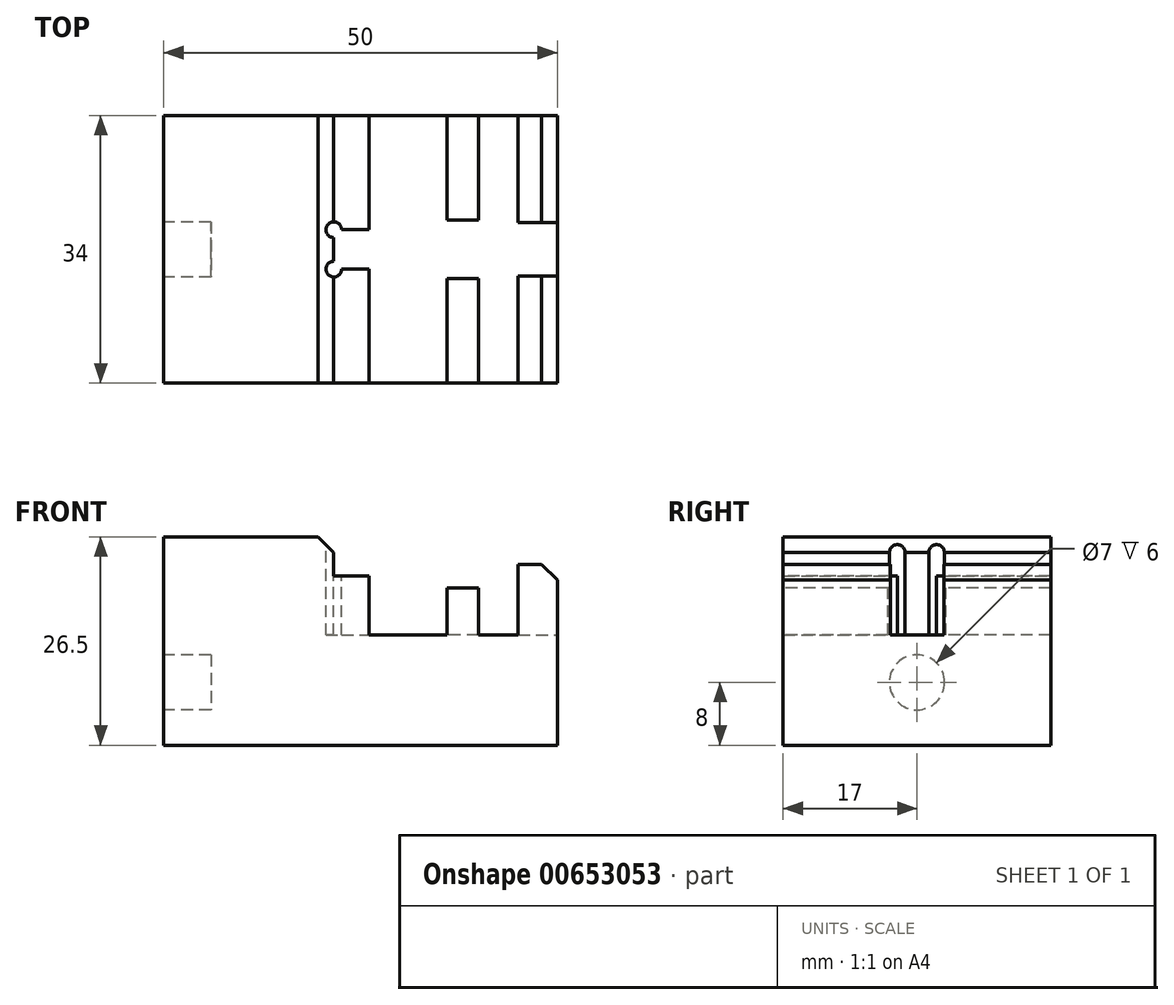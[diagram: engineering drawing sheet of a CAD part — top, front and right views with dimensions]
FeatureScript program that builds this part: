
annotation { "Feature Type Name" : "Feature", "Feature Type Description" : "" }
export const myFeature = defineFeature(function(context is Context, id is Id, definition is map)
    precondition{}
    {
        {
            var Q0;
            Q0=qCreatedBy(makeId("Front.planeOp"),FACE);
            var sketch = newSketch(context, id + "F0", { "sketchPlane" : qUnion([Q0])});
            skLineSegment(sketch, "E0.bottom", {"start": v(-25, 13) * mm, "end": v(-3.4, 13) * mm});
            skLineSegment(sketch, "E0.top", {"start": v(-25, -13) * mm, "end": v(25, -13) * mm});
            skLineSegment(sketch, "E0.left", {"start": v(-25, 13) * mm, "end": v(-25, -13) * mm});
            skLineSegment(sketch, "E0.right", {"start": v(25, 10) * mm, "end": v(25, -13) * mm});
            skPoint(sketch, "E0.middle", {"position": v(0, 0) * mm});
            skLineSegment(sketch, "E1.0", {"start": v(-3.4, 13) * mm, "end": v(-3.4, 1) * mm});
            skLineSegment(sketch, "E2.0", {"start": v(-3.4, 1) * mm, "end": v(20, 1) * mm});
            skLineSegment(sketch, "E3.0", {"start": v(20, 10) * mm, "end": v(20, 1) * mm});
            skPoint(sketch, "E4.orphan", {"position": v(25, 13) * mm});
            skLineSegment(sketch, "E5.trimOffspring", {"start": v(20, 10) * mm, "end": v(25, 10) * mm});
            skSolve(sketch);
        }
        {
            var Q0;
            Q0=qSketchRegion(id+"F0",true);
            extrude(context, id + "F1", {"entities" : qUnion([Q0]), "depth" : 34 * mm, "offsetDistance" : 25 * mm});
        }
        {
            var Q0;
            Q0=makeQuery(id+"F1.opExtrude","SWEPT_FACE",FACE,{"disambiguationData":[OSD([sQuery(id+"F0.wireOp",EDGE,"E0.right")])]});
            var sketch = newSketch(context, id + "F2", { "sketchPlane" : qUnion([Q0])});
            skLineSegment(sketch, "E6.bottom", {"start": v(-20.4, 10) * mm, "end": v(-13.6, 10) * mm});
            skLineSegment(sketch, "E6.top", {"start": v(-20.4, 1) * mm, "end": v(-13.6, 1) * mm});
            skLineSegment(sketch, "E6.left", {"start": v(-20.4, 10) * mm, "end": v(-20.4, 1) * mm});
            skLineSegment(sketch, "E6.right", {"start": v(-13.6, 10) * mm, "end": v(-13.6, 1) * mm});
            skSolve(sketch);
        }
        {
            var Q0;
            Q0=qSketchRegion(id+"F2",true);
            var Q1;
            Q1=makeQuery(id+"F1.opExtrude","SWEPT_FACE",FACE,{"disambiguationData":[OSD([sQuery(id+"F0.wireOp",EDGE,"E3.0")])]});
            extrude(context, id + "F3", {"entities" : qUnion([Q0]), "operationType" : NewBodyOperationType.REMOVE, "endBound" : BoundingType.UP_TO_SURFACE, "oppositeDirection" : true, "depth" : 25 * mm, "endBoundEntityFace" : qUnion([Q1]), "offsetDistance" : 25 * mm});
        }
        {
            var Q0;
            Q0=makeQuery(id+"F1.opExtrude","SWEPT_FACE",FACE,{"disambiguationData":[OSD([sQuery(id+"F0.wireOp",EDGE,"E0.left")])]});
            var sketch = newSketch(context, id + "F4", { "sketchPlane" : qUnion([Q0])});
            skCircle(sketch, "E7", {"center": v(17, -5) * mm, "radius": 3.5 * mm});
            skSolve(sketch);
        }
        {
            var Q0;
            Q0=qSketchRegion(id+"F4",true);
            extrude(context, id + "F5", {"entities" : qUnion([Q0]), "operationType" : NewBodyOperationType.REMOVE, "oppositeDirection" : true, "depth" : 6 * mm, "offsetDistance" : 25 * mm});
        }
        {
            var Q0;
            Q0=makeQuery(id+"F3.boolean.opBoolean","MERGE",FACE,{"derivedFrom":[makeQuery(id+"F1.opExtrude","SWEPT_FACE",FACE,{"disambiguationData":[OSD([sQuery(id+"F0.wireOp",EDGE,"E2.0")])]}),makeQuery(id+"F3.opExtrude","SWEPT_FACE",FACE,{"disambiguationData":[OSD([sQuery(id+"F2.wireOp",EDGE,"E6.top")])]})]});
            var sketch = newSketch(context, id + "F6", { "sketchPlane" : qUnion([Q0])});
            skLineSegment(sketch, "E8.bottom", {"start": v(-3.4, -34) * mm, "end": v(1.1, -34) * mm});
            skLineSegment(sketch, "E8.top", {"start": v(-3.4, -19.5) * mm, "end": v(1.1, -19.5) * mm});
            skLineSegment(sketch, "E8.left", {"start": v(-3.4, -34) * mm, "end": v(-3.4, -19.5) * mm});
            skLineSegment(sketch, "E8.right", {"start": v(1.1, -34) * mm, "end": v(1.1, -19.5) * mm});
            skLineSegment(sketch, "E9.bottom", {"start": v(-3.4, 0) * mm, "end": v(1.1, 0) * mm});
            skLineSegment(sketch, "E9.top", {"start": v(-3.4, -14.5) * mm, "end": v(1.1, -14.5) * mm});
            skLineSegment(sketch, "E9.left", {"start": v(-3.4, 0) * mm, "end": v(-3.4, -14.5) * mm});
            skLineSegment(sketch, "E9.right", {"start": v(1.1, 0) * mm, "end": v(1.1, -14.5) * mm});
            skSolve(sketch);
        }
        {
            var Q0;
            Q0 = qSketchRegion(id + "F6", true);
            var Q1;
            Q1=makeQuery(id+"F1.opExtrude","SWEPT_FACE",FACE,{"disambiguationData":[OSD([sQuery(id+"F0.wireOp",EDGE,"E0.bottom")])]});
            extrude(context, id + "F7", {"entities" : qUnion([Q0]), "operationType" : NewBodyOperationType.ADD, "endBound" : BoundingType.UP_TO_SURFACE, "depth" : 25 * mm, "endBoundEntityFace" : qUnion([Q1]), "offsetDistance" : 25 * mm});
        }
        {
            var Q0;
            {var subQ0=sQuery(id+"F0.wireOp",EDGE,"E0.bottom");Q0=makeQuery(id+"F7.boolean.opBoolean","MERGE",FACE,{"derivedFrom":[makeQuery(id+"F1.opExtrude","SWEPT_FACE",FACE,{"disambiguationData":[OSD([subQ0])]}),makeQuery(id+"F7.opExtrude","CAP_FACE",FACE,{"disambiguationData":[OSD([subQ0]),OD(0.0)],"isStart":false}),makeQuery(id+"F7.opExtrude","CAP_FACE",FACE,{"disambiguationData":[OSD([subQ0]),OD(1.0)],"isStart":false})]});}
            var sketch = newSketch(context, id + "F8", { "sketchPlane" : qUnion([Q0])});
            skLineSegment(sketch, "E10.top", {"start": v(1.1, -21.7) * mm, "end": v(11, -21.7) * mm});
            skLineSegment(sketch, "E11.top", {"start": v(1.1, -12.3) * mm, "end": v(11, -12.3) * mm});
            skLineSegment(sketch, "E12.top", {"start": v(1.1, -34) * mm, "end": v(11, -34) * mm});
            skLineSegment(sketch, "E12.left", {"start": v(1.1, -21.7) * mm, "end": v(1.1, -34) * mm});
            skLineSegment(sketch, "E12.right", {"start": v(11, -21.7) * mm, "end": v(11, -34) * mm});
            skLineSegment(sketch, "E13.top", {"start": v(1.1, 0) * mm, "end": v(11, 0) * mm});
            skLineSegment(sketch, "E13.left", {"start": v(1.1, -12.3) * mm, "end": v(1.1, 0) * mm});
            skLineSegment(sketch, "E13.right", {"start": v(11, -12.3) * mm, "end": v(11, 0) * mm});
            skSolve(sketch);
        }
        {
            var Q0;
            Q0 = qSketchRegion(id + "F8", true);
            var Q1;
            Q1=makeQuery(id+"F3.boolean.opBoolean","MERGE",FACE,{"derivedFrom":[makeQuery(id+"F1.opExtrude","SWEPT_FACE",FACE,{"disambiguationData":[OSD([sQuery(id+"F0.wireOp",EDGE,"E2.0")])]}),makeQuery(id+"F3.opExtrude","SWEPT_FACE",FACE,{"disambiguationData":[OSD([sQuery(id+"F2.wireOp",EDGE,"E6.top")])]})]});
            extrude(context, id + "F9", {"entities" : qUnion([Q0]), "operationType" : NewBodyOperationType.ADD, "endBound" : BoundingType.UP_TO_SURFACE, "oppositeDirection" : true, "depth" : 25 * mm, "endBoundEntityFace" : qUnion([Q1]), "offsetDistance" : 25 * mm});
        }
        {
            var Q0;
            {var subQ0=sQuery(id+"F0.wireOp",EDGE,"E0.bottom");Q0=makeQuery(id+"F9.boolean.opBoolean","MERGE",FACE,{"derivedFrom":[makeQuery(id+"F7.boolean.opBoolean","MERGE",FACE,{"derivedFrom":[makeQuery(id+"F1.opExtrude","SWEPT_FACE",FACE,{"disambiguationData":[OSD([subQ0])]}),makeQuery(id+"F7.opExtrude","CAP_FACE",FACE,{"disambiguationData":[OSD([subQ0]),OD(0.0)],"isStart":false}),makeQuery(id+"F7.opExtrude","CAP_FACE",FACE,{"disambiguationData":[OSD([subQ0]),OD(1.0)],"isStart":false})]}),makeQuery(id+"F9.opExtrude","CAP_FACE",FACE,{"disambiguationData":[OSD([sQuery(id+"F8.wireOp",EDGE,"E10.top"),sQuery(id+"F8.wireOp",EDGE,"E12.top"),sQuery(id+"F8.wireOp",EDGE,"E12.left"),sQuery(id+"F8.wireOp",EDGE,"E12.right")])],"isStart":true}),makeQuery(id+"F9.opExtrude","CAP_FACE",FACE,{"disambiguationData":[OSD([sQuery(id+"F8.wireOp",EDGE,"E11.top"),sQuery(id+"F8.wireOp",EDGE,"E13.top"),sQuery(id+"F8.wireOp",EDGE,"E13.left"),sQuery(id+"F8.wireOp",EDGE,"E13.right")])],"isStart":true})]});}
            var sketch = newSketch(context, id + "F10", { "sketchPlane" : qUnion([Q0])});
            skLineSegment(sketch, "E14.bottom", {"start": v(11, -34) * mm, "end": v(15, -34) * mm});
            skLineSegment(sketch, "E14.top", {"start": v(11, -20.7) * mm, "end": v(15, -20.7) * mm});
            skLineSegment(sketch, "E14.left", {"start": v(11, -34) * mm, "end": v(11, -20.7) * mm});
            skLineSegment(sketch, "E14.right", {"start": v(15, -34) * mm, "end": v(15, -20.7) * mm});
            skLineSegment(sketch, "E15.MirrorCS", {"start": v(11, 0) * mm, "end": v(11, -13.3) * mm});
            skLineSegment(sketch, "E16.MirrorCS", {"start": v(15, 0) * mm, "end": v(15, -13.3) * mm});
            skLineSegment(sketch, "E17.MirrorCS", {"start": v(11, -13.3) * mm, "end": v(15, -13.3) * mm});
            skLineSegment(sketch, "E18.MirrorCS", {"start": v(11, 0) * mm, "end": v(15, 0) * mm});
            skSolve(sketch);
        }
        {
            var Q0;
            Q0 = qSketchRegion(id + "F10", true);
            var Q1;
            Q1=makeQuery(id+"F3.boolean.opBoolean","MERGE",FACE,{"derivedFrom":[makeQuery(id+"F1.opExtrude","SWEPT_FACE",FACE,{"disambiguationData":[OSD([sQuery(id+"F0.wireOp",EDGE,"E2.0")])]}),makeQuery(id+"F3.opExtrude","SWEPT_FACE",FACE,{"disambiguationData":[OSD([sQuery(id+"F2.wireOp",EDGE,"E6.top")])]})]});
            extrude(context, id + "F11", {"entities" : qUnion([Q0]), "operationType" : NewBodyOperationType.ADD, "endBound" : BoundingType.UP_TO_SURFACE, "oppositeDirection" : true, "depth" : 25 * mm, "endBoundEntityFace" : qUnion([Q1]), "offsetDistance" : 25 * mm});
        }
        {
            var Q0;
            Q0=makeQuery(id+"F11.boolean.opBoolean","MERGE",FACE,{"derivedFrom":[makeQuery(id+"F9.boolean.opBoolean","MERGE",FACE,{"derivedFrom":[makeQuery(id+"F7.boolean.opBoolean","MERGE",FACE,{"derivedFrom":[makeQuery(id+"F1.opExtrude","CAP_FACE",FACE,{"disambiguationData":[OSD([sQuery(id+"F0.wireOp",EDGE,"E0.bottom"),sQuery(id+"F0.wireOp",EDGE,"E0.top"),sQuery(id+"F0.wireOp",EDGE,"E0.left"),sQuery(id+"F0.wireOp",EDGE,"E0.right"),sQuery(id+"F0.wireOp",EDGE,"E1.0"),sQuery(id+"F0.wireOp",EDGE,"E2.0"),sQuery(id+"F0.wireOp",EDGE,"E3.0"),sQuery(id+"F0.wireOp",EDGE,"E5.trimOffspring")])],"isStart":false}),makeQuery(id+"F7.opExtrude","SWEPT_FACE",FACE,{"disambiguationData":[OSD([sQuery(id+"F6.wireOp",EDGE,"E8.bottom")])]})]}),makeQuery(id+"F9.opExtrude","SWEPT_FACE",FACE,{"disambiguationData":[OSD([sQuery(id+"F8.wireOp",EDGE,"E12.top")])]})]}),makeQuery(id+"F11.opExtrude","SWEPT_FACE",FACE,{"disambiguationData":[OSD([sQuery(id+"F10.wireOp",EDGE,"E14.bottom")])]})]});
            var sketch = newSketch(context, id + "F12", { "sketchPlane" : qUnion([Q0])});
            skLineSegment(sketch, "E19.bottom", {"start": v(15, 13) * mm, "end": v(1.1, 13) * mm});
            skLineSegment(sketch, "E19.top", {"start": v(15, 7) * mm, "end": v(1.1, 7) * mm});
            skLineSegment(sketch, "E19.left", {"start": v(15, 13) * mm, "end": v(15, 7) * mm});
            skLineSegment(sketch, "E20.0", {"start": v(1.1, 7) * mm, "end": v(1.1, 13) * mm});
            skPoint(sketch, "E21.orphan", {"position": v(1.1, 1) * mm});
            skSolve(sketch);
        }
        {
            var Q0;
            Q0 = qSketchRegion(id + "F12", true);
            extrude(context, id + "F13", {"entities" : qUnion([Q0]), "operationType" : NewBodyOperationType.REMOVE, "endBound" : BoundingType.THROUGH_ALL, "oppositeDirection" : true, "depth" : 25 * mm, "offsetDistance" : 25 * mm});
        }
        {
            var Q0;
            Q0=makeQuery(id+"F11.boolean.opBoolean","MERGE",FACE,{"derivedFrom":[makeQuery(id+"F9.boolean.opBoolean","MERGE",FACE,{"derivedFrom":[makeQuery(id+"F7.boolean.opBoolean","MERGE",FACE,{"derivedFrom":[makeQuery(id+"F1.opExtrude","CAP_FACE",FACE,{"disambiguationData":[OSD([sQuery(id+"F0.wireOp",EDGE,"E0.bottom"),sQuery(id+"F0.wireOp",EDGE,"E0.top"),sQuery(id+"F0.wireOp",EDGE,"E0.left"),sQuery(id+"F0.wireOp",EDGE,"E0.right"),sQuery(id+"F0.wireOp",EDGE,"E1.0"),sQuery(id+"F0.wireOp",EDGE,"E2.0"),sQuery(id+"F0.wireOp",EDGE,"E3.0"),sQuery(id+"F0.wireOp",EDGE,"E5.trimOffspring")])],"isStart":false}),makeQuery(id+"F7.opExtrude","SWEPT_FACE",FACE,{"disambiguationData":[OSD([sQuery(id+"F6.wireOp",EDGE,"E8.bottom")])]})]}),makeQuery(id+"F9.opExtrude","SWEPT_FACE",FACE,{"disambiguationData":[OSD([sQuery(id+"F8.wireOp",EDGE,"E12.top")])]})]}),makeQuery(id+"F11.opExtrude","SWEPT_FACE",FACE,{"disambiguationData":[OSD([sQuery(id+"F10.wireOp",EDGE,"E14.bottom")])]})]});
            var sketch = newSketch(context, id + "F14", { "sketchPlane" : qUnion([Q0])});
            skLineSegment(sketch, "E22.0", {"start": v(11, 1) * mm, "end": v(11, 7) * mm});
            skLineSegment(sketch, "E23.0", {"start": v(1.1, 7) * mm, "end": v(1.1, 1) * mm});
            skLineSegment(sketch, "E24", {"start": v(11, 1) * mm, "end": v(1.1, 1) * mm});
            skLineSegment(sketch, "E25", {"start": v(11, 7) * mm, "end": v(1.1, 7) * mm});
            skPoint(sketch, "E26.orphan", {"position": v(1.1, 11) * mm});
            skSolve(sketch);
        }
        {
            var Q0;
            Q0 = qSketchRegion(id + "F14", true);
            extrude(context, id + "F15", {"entities" : qUnion([Q0]), "operationType" : NewBodyOperationType.REMOVE, "endBound" : BoundingType.THROUGH_ALL, "oppositeDirection" : true, "depth" : 25 * mm, "offsetDistance" : 25 * mm});
        }
        {
            var Q0;
            Q0=makeQuery(id+"F11.boolean.opBoolean","MERGE",FACE,{"derivedFrom":[makeQuery(id+"F9.boolean.opBoolean","MERGE",FACE,{"derivedFrom":[makeQuery(id+"F7.boolean.opBoolean","MERGE",FACE,{"derivedFrom":[makeQuery(id+"F1.opExtrude","CAP_FACE",FACE,{"disambiguationData":[OSD([sQuery(id+"F0.wireOp",EDGE,"E0.bottom"),sQuery(id+"F0.wireOp",EDGE,"E0.top"),sQuery(id+"F0.wireOp",EDGE,"E0.left"),sQuery(id+"F0.wireOp",EDGE,"E0.right"),sQuery(id+"F0.wireOp",EDGE,"E1.0"),sQuery(id+"F0.wireOp",EDGE,"E2.0"),sQuery(id+"F0.wireOp",EDGE,"E3.0"),sQuery(id+"F0.wireOp",EDGE,"E5.trimOffspring")])],"isStart":false}),makeQuery(id+"F7.opExtrude","SWEPT_FACE",FACE,{"disambiguationData":[OSD([sQuery(id+"F6.wireOp",EDGE,"E8.bottom")])]})]}),makeQuery(id+"F9.opExtrude","SWEPT_FACE",FACE,{"disambiguationData":[OSD([sQuery(id+"F8.wireOp",EDGE,"E12.top")])]})]}),makeQuery(id+"F11.opExtrude","SWEPT_FACE",FACE,{"disambiguationData":[OSD([sQuery(id+"F10.wireOp",EDGE,"E14.bottom")])]})]});
            var sketch = newSketch(context, id + "F16", { "sketchPlane" : qUnion([Q0])});
            skLineSegment(sketch, "E27.bottom", {"start": v(-25, 13) * mm, "end": v(1.1, 13) * mm});
            skLineSegment(sketch, "E27.top", {"start": v(-25, 8.5) * mm, "end": v(1.1, 8.5) * mm});
            skLineSegment(sketch, "E27.left", {"start": v(-25, 13) * mm, "end": v(-25, 8.5) * mm});
            skLineSegment(sketch, "E27.right", {"start": v(1.1, 13) * mm, "end": v(1.1, 8.5) * mm});
            skSolve(sketch);
        }
        {
            var Q0;
            Q0 = qSketchRegion(id + "F16", true);
            extrude(context, id + "F17", {"entities" : qUnion([Q0]), "operationType" : NewBodyOperationType.REMOVE, "endBound" : BoundingType.THROUGH_ALL, "oppositeDirection" : true, "depth" : 25 * mm, "offsetDistance" : 25 * mm});
        }
        {
            var Q0;
            {var subQ0=sQuery(id+"F0.wireOp",EDGE,"E0.bottom");Q0=makeQuery(id+"F13.boolean.opBoolean","MERGE",EDGE,{"derivedFrom":[makeQuery(id+"F7.opExtrude","TWEAK_EDGE",EDGE,{"derivedFrom":[makeQuery(id+"F1.opExtrude","SWEPT_FACE",FACE,{"disambiguationData":[OSD([subQ0])]}),makeQuery(id+"F6.imprint","IMPRINT",EDGE,{"derivedFrom":sQuery(id+"F6.wireOp",EDGE,"E9.right")})]}),makeQuery(id+"F13.opExtrude","SWEPT_EDGE",EDGE,{"disambiguationData":[OSD([subQ0,sQuery(id+"F6.wireOp",EDGE,"E8.bottom"),sQuery(id+"F8.wireOp",EDGE,"E12.top"),sQuery(id+"F10.wireOp",EDGE,"E14.bottom"),sQuery(id+"F12.wireOp",EDGE,"E19.bottom"),sQuery(id+"F12.wireOp",EDGE,"E20.0")])]})]});}
            var Q1;
            {var subQ0=sQuery(id+"F0.wireOp",EDGE,"E0.bottom");Q1=makeQuery(id+"F13.boolean.opBoolean","MERGE",EDGE,{"derivedFrom":[makeQuery(id+"F7.opExtrude","TWEAK_EDGE",EDGE,{"derivedFrom":[makeQuery(id+"F1.opExtrude","SWEPT_FACE",FACE,{"disambiguationData":[OSD([subQ0])]}),makeQuery(id+"F6.imprint","IMPRINT",EDGE,{"derivedFrom":sQuery(id+"F6.wireOp",EDGE,"E8.right")})]}),makeQuery(id+"F13.opExtrude","SWEPT_EDGE",EDGE,{"disambiguationData":[OSD([subQ0,sQuery(id+"F6.wireOp",EDGE,"E8.bottom"),sQuery(id+"F8.wireOp",EDGE,"E12.top"),sQuery(id+"F10.wireOp",EDGE,"E14.bottom"),sQuery(id+"F12.wireOp",EDGE,"E19.bottom"),sQuery(id+"F12.wireOp",EDGE,"E20.0")])]})]});}
            var Q2;
            {var subQ0=sQuery(id+"F10.wireOp",EDGE,"E14.right");var subQ1=sQuery(id+"F12.wireOp",EDGE,"E19.top");Q2=makeQuery(id+"F13.boolean.opBoolean","COPY",EDGE,{"disambiguationData":[topologyDisambiguationEdgeConnected([makeQuery(id+"F11.opExtrude","SWEPT_FACE",FACE,{"disambiguationData":[OSD([subQ0])]})])],"derivedFrom":makeQuery(id+"F13.opExtrude","SWEPT_EDGE",EDGE,{"disambiguationData":[OSD([sQuery(id+"F10.wireOp",EDGE,"E14.bottom"),subQ0,subQ1,sQuery(id+"F12.wireOp",EDGE,"E19.left")])]})});}
            var Q3;
            {var subQ0=sQuery(id+"F12.wireOp",EDGE,"E19.top");Q3=makeQuery(id+"F13.boolean.opBoolean","COPY",EDGE,{"disambiguationData":[topologyDisambiguationEdgeConnected([makeQuery(id+"F11.opExtrude","SWEPT_FACE",FACE,{"disambiguationData":[OSD([sQuery(id+"F10.wireOp",EDGE,"E16.MirrorCS")])]})])],"derivedFrom":makeQuery(id+"F13.opExtrude","SWEPT_EDGE",EDGE,{"disambiguationData":[OSD([sQuery(id+"F10.wireOp",EDGE,"E14.bottom"),sQuery(id+"F10.wireOp",EDGE,"E14.right"),subQ0,sQuery(id+"F12.wireOp",EDGE,"E19.left")])]})});}
            var Q4;
            {var subQ0=sQuery(id+"F0.wireOp",EDGE,"E5.trimOffspring");var subQ1=sQuery(id+"F0.wireOp",EDGE,"E0.right");Q4=makeQuery(id+"F3.boolean.opBoolean","SPLIT",EDGE,{"disambiguationData":[TD([makeQuery(id+"F3.opExtrude","SWEPT_FACE",FACE,{"disambiguationData":[OSD([sQuery(id+"F2.wireOp",EDGE,"E6.right")])]})])],"derivedFrom":makeQuery(id+"F1.opExtrude","SWEPT_EDGE",EDGE,{"disambiguationData":[OSD([subQ1,subQ0])]})});}
            var Q5;
            {var subQ0=sQuery(id+"F0.wireOp",EDGE,"E5.trimOffspring");var subQ1=sQuery(id+"F0.wireOp",EDGE,"E0.right");Q5=makeQuery(id+"F3.boolean.opBoolean","SPLIT",EDGE,{"disambiguationData":[TD([makeQuery(id+"F3.opExtrude","SWEPT_FACE",FACE,{"disambiguationData":[OSD([sQuery(id+"F2.wireOp",EDGE,"E6.left")])]})])],"derivedFrom":makeQuery(id+"F1.opExtrude","SWEPT_EDGE",EDGE,{"disambiguationData":[OSD([subQ1,subQ0])]})});}
            var Q6;
            {var subQ0=sQuery(id+"F12.wireOp",EDGE,"E20.0");var subQ1=sQuery(id+"F16.wireOp",EDGE,"E27.top");var subQ2=sQuery(id+"F14.wireOp",EDGE,"E23.0");Q6=makeQuery(id+"F17.boolean.opBoolean","COPY",EDGE,{"disambiguationData":[topologyDisambiguationEdgeConnected([makeQuery(id+"F7.opExtrude","SWEPT_FACE",FACE,{"disambiguationData":[OSD([sQuery(id+"F6.wireOp",EDGE,"E9.right")])]})])],"derivedFrom":makeQuery(id+"F17.opExtrude","SWEPT_EDGE",EDGE,{"disambiguationData":[OSD([subQ0,subQ2,subQ1,sQuery(id+"F16.wireOp",EDGE,"E27.right")])]})});}
            var Q7;
            {var subQ0=sQuery(id+"F12.wireOp",EDGE,"E20.0");var subQ1=sQuery(id+"F16.wireOp",EDGE,"E27.top");var subQ2=sQuery(id+"F14.wireOp",EDGE,"E23.0");Q7=makeQuery(id+"F17.boolean.opBoolean","COPY",EDGE,{"disambiguationData":[topologyDisambiguationEdgeConnected([makeQuery(id+"F7.opExtrude","SWEPT_FACE",FACE,{"disambiguationData":[OSD([sQuery(id+"F6.wireOp",EDGE,"E8.right")])]})])],"derivedFrom":makeQuery(id+"F17.opExtrude","SWEPT_EDGE",EDGE,{"disambiguationData":[OSD([subQ0,subQ2,subQ1,sQuery(id+"F16.wireOp",EDGE,"E27.right")])]})});}
            chamfer(context, id + "F18", {"entities" : qUnion([Q0, Q1, Q2, Q3, Q4, Q5, Q6, Q7]), "width" : 2 * mm, "tangentPropagation" : true});
        }
        {
            var Q0;
            Q0=makeQuery(id+"F17.boolean.opBoolean","COPY",FACE,{"derivedFrom":makeQuery(id+"F17.opExtrude","SWEPT_FACE",FACE,{"disambiguationData":[OSD([sQuery(id+"F16.wireOp",EDGE,"E27.top")])]})});
            var sketch = newSketch(context, id + "F19", { "sketchPlane" : qUnion([Q0])});
            skLineSegment(sketch, "E28.bottom", {"start": v(-3.4, -34) * mm, "end": v(-25, -34) * mm});
            skLineSegment(sketch, "E28.top", {"start": v(-3.4, 0) * mm, "end": v(-25, 0) * mm});
            skLineSegment(sketch, "E28.left", {"start": v(-3.4, -34) * mm, "end": v(-3.4, 0) * mm});
            skLineSegment(sketch, "E28.right", {"start": v(-25, -34) * mm, "end": v(-25, 0) * mm});
            skSolve(sketch);
        }
        {
            var Q0;
            Q0 = qSketchRegion(id + "F19", true);
            extrude(context, id + "F20", {"entities" : qUnion([Q0]), "operationType" : NewBodyOperationType.ADD, "depth" : 5 * mm, "offsetDistance" : 25 * mm});
        }
        {
            var Q0;
            Q0=makeQuery(id+"F20.opExtrude","CAP_FACE",FACE,{"disambiguationData":[OSD([sQuery(id+"F19.wireOp",EDGE,"E28.bottom"),sQuery(id+"F19.wireOp",EDGE,"E28.top"),sQuery(id+"F19.wireOp",EDGE,"E28.left"),sQuery(id+"F19.wireOp",EDGE,"E28.right")])],"isStart":false});
            var sketch = newSketch(context, id + "F21", { "sketchPlane" : qUnion([Q0])});
            skCircle(sketch, "E29", {"center": v(-3.4, -19.5) * mm, "radius": 1 * mm});
            skCircle(sketch, "E30", {"center": v(-3.4, -14.5) * mm, "radius": 1 * mm});
            skSolve(sketch);
        }
        {
            var Q0;
            Q0 = qSketchRegion(id + "F21", true);
            var Q1;
            Q1=makeQuery(id+"F3.boolean.opBoolean","MERGE",FACE,{"derivedFrom":[makeQuery(id+"F1.opExtrude","SWEPT_FACE",FACE,{"disambiguationData":[OSD([sQuery(id+"F0.wireOp",EDGE,"E2.0")])]}),makeQuery(id+"F3.opExtrude","SWEPT_FACE",FACE,{"disambiguationData":[OSD([sQuery(id+"F2.wireOp",EDGE,"E6.top")])]})]});
            extrude(context, id + "F22", {"entities" : qUnion([Q0]), "operationType" : NewBodyOperationType.REMOVE, "endBound" : BoundingType.UP_TO_SURFACE, "oppositeDirection" : true, "depth" : 25 * mm, "endBoundEntityFace" : qUnion([Q1]), "offsetDistance" : 25 * mm});
        }
        {
            var Q0;
            {var subQ0=sQuery(id+"F0.wireOp",EDGE,"E1.0");var subQ1=sQuery(id+"F19.wireOp",EDGE,"E28.left");var subQ2=sQuery(id+"F19.wireOp",EDGE,"E28.top");Q0=makeQuery(id+"F22.boolean.opBoolean","SPLIT",EDGE,{"disambiguationData":[TD([makeQuery(id+"F1.opExtrude","CAP_FACE",FACE,{"disambiguationData":[OSD([sQuery(id+"F0.wireOp",EDGE,"E0.bottom"),sQuery(id+"F0.wireOp",EDGE,"E0.top"),sQuery(id+"F0.wireOp",EDGE,"E0.left"),sQuery(id+"F0.wireOp",EDGE,"E0.right"),subQ0,sQuery(id+"F0.wireOp",EDGE,"E2.0"),sQuery(id+"F0.wireOp",EDGE,"E3.0"),sQuery(id+"F0.wireOp",EDGE,"E5.trimOffspring")])],"isStart":true}),makeQuery(id+"F1.opExtrude","SWEPT_FACE",FACE,{"disambiguationData":[OSD([subQ0])]}),makeQuery(id+"F7.opExtrude","SWEPT_FACE",FACE,{"disambiguationData":[OSD([sQuery(id+"F6.wireOp",EDGE,"E9.bottom")])]}),makeQuery(id+"F9.opExtrude","SWEPT_FACE",FACE,{"disambiguationData":[OSD([sQuery(id+"F8.wireOp",EDGE,"E13.top")])]}),makeQuery(id+"F11.opExtrude","SWEPT_FACE",FACE,{"disambiguationData":[OSD([sQuery(id+"F10.wireOp",EDGE,"E18.MirrorCS")])]}),makeQuery(id+"F20.opExtrude","CAP_FACE",FACE,{"disambiguationData":[OSD([sQuery(id+"F19.wireOp",EDGE,"E28.bottom"),subQ2,subQ1,sQuery(id+"F19.wireOp",EDGE,"E28.right")])],"isStart":false}),makeQuery(id+"F20.opExtrude","SWEPT_FACE",FACE,{"disambiguationData":[OSD([subQ2])]}),makeQuery(id+"F20.opExtrude","SWEPT_FACE",FACE,{"disambiguationData":[OSD([subQ1])]}),makeQuery(id+"F22.opExtrude","SWEPT_FACE",FACE,{"disambiguationData":[OSD([sQuery(id+"F21.wireOp",EDGE,"E30")])]})])],"derivedFrom":makeQuery(id+"F20.opExtrude","CAP_EDGE",EDGE,{"disambiguationData":[OSD([subQ1])],"isStart":false})});}
            chamfer(context, id + "F23", {"entities" : qUnion([Q0]), "width" : 2 * mm, "tangentPropagation" : true});
        }
    });
